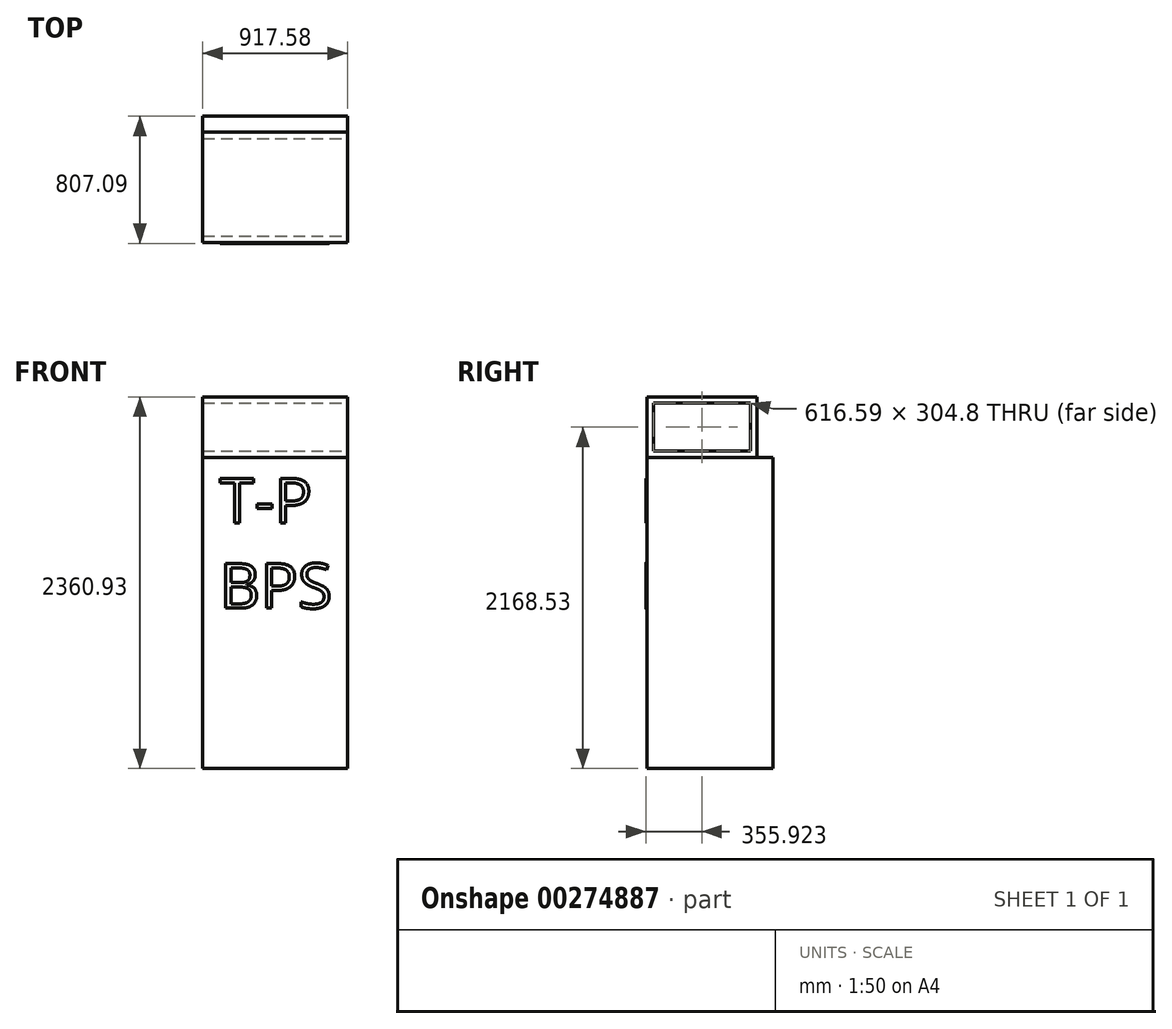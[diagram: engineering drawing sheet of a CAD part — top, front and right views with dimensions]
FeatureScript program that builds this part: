
annotation { "Feature Type Name" : "Feature", "Feature Type Description" : "" }
export const myFeature = defineFeature(function(context is Context, id is Id, definition is map)
    precondition{}
    {
        {
            var Q0;
            Q0=qCreatedBy(makeId("Top.planeOp"),FACE);
            var sketch = newSketch(context, id + "F0", { "sketchPlane" : qUnion([Q0])});
            skLineSegment(sketch, "E0.bottom", {"start": v(0, 0) * mm, "end": v(917.58, 0) * mm});
            skLineSegment(sketch, "E0.top", {"start": v(0, -800.74) * mm, "end": v(917.58, -800.74) * mm});
            skLineSegment(sketch, "E0.left", {"start": v(0, 0) * mm, "end": v(0, -800.74) * mm});
            skLineSegment(sketch, "E0.right", {"start": v(917.58, 0) * mm, "end": v(917.58, -800.74) * mm});
            skSolve(sketch);
        }
        {
            var Q0;
            Q0=makeQuery(id+"F0.imprint","IMPRINT",FACE,{"disambiguationData":[TD([[makeQuery(id+"F0.imprint","IMPRINT",EDGE,{"derivedFrom":sQuery(id+"F0.wireOp",EDGE,"E0.bottom")}),-1.0]])]});
            extrude(context, id + "F1", {"entities" : qUnion([Q0]), "depth" : 1974.85 * mm});
        }
        {
            var Q0;
            Q0=makeQuery(id+"F1.opExtrude","SWEPT_FACE",FACE,{"disambiguationData":[OSD([sQuery(id+"F0.wireOp",EDGE,"E0.top")])]});
            var sketch = newSketch(context, id + "F2", { "sketchPlane" : qUnion([Q0])});
            skText(sketch, "E1", { "text": "T-P\nBPS", "fontName": "OpenSans-Regular.ttf"});
            const initialGuessF2  = {"E1": [0.10689, 1.55914, 1, 0, 0.28607]};
            skSetInitialGuess(sketch, initialGuessF2);
            skSolve(sketch);
        }
        {
            var Q0;
            Q0 = qSketchRegion(id + "F2", true);
            extrude(context, id + "F3", {"entities" : qUnion([Q0]), "operationType" : NewBodyOperationType.ADD, "depth" : 6.35 * mm});
        }
        {
            var Q0;
            Q0=makeQuery(id+"F1.opExtrude","CAP_FACE",FACE,{"disambiguationData":[OSD([sQuery(id+"F0.wireOp",EDGE,"E0.bottom"),sQuery(id+"F0.wireOp",EDGE,"E0.top"),sQuery(id+"F0.wireOp",EDGE,"E0.left"),sQuery(id+"F0.wireOp",EDGE,"E0.right")])],"isStart":false});
            var sketch = newSketch(context, id + "F4", { "sketchPlane" : qUnion([Q0])});
            skLineSegment(sketch, "E2.bottom", {"start": v(0, 0) * mm, "end": v(917.58, 0) * mm});
            skLineSegment(sketch, "E2.top", {"start": v(0, -800.74) * mm, "end": v(917.58, -800.74) * mm});
            skLineSegment(sketch, "E2.left", {"start": v(0, 0) * mm, "end": v(0, -800.74) * mm});
            skLineSegment(sketch, "E2.right", {"start": v(917.58, 0) * mm, "end": v(917.58, -800.74) * mm});
            skSolve(sketch);
        }
        {
            var Q0;
            Q0=makeQuery(id+"F4.imprint","IMPRINT",FACE,{"disambiguationData":[TD([[makeQuery(id+"F4.imprint","IMPRINT",EDGE,{"derivedFrom":sQuery(id+"F4.wireOp",EDGE,"E2.bottom")}),-1.0]])]});
            extrude(context, id + "F5", {"entities" : qUnion([Q0]), "depth" : 508 * mm, "offsetDistance" : 25.4 * mm});
        }
        {
            var Q0;
            Q0=makeQuery(id+"F1.opExtrude","SWEPT_FACE",FACE,{"disambiguationData":[OSD([sQuery(id+"F0.wireOp",EDGE,"E0.right")])]});
            var sketch = newSketch(context, id + "F6", { "sketchPlane" : qUnion([Q0])});
            skLineSegment(sketch, "E3", {"start": v(0, 0) * mm, "end": v(0, 2016.13) * mm, "construction": true});
            skLineSegment(sketch, "E4", {"start": v(0, 2016.13) * mm, "end": v(-41.28, 2016.13) * mm, "construction": true});
            skLineSegment(sketch, "E5.bottom", {"start": v(-800.74, 1974.85) * mm, "end": v(-759.46, 1974.85) * mm, "construction": true});
            skLineSegment(sketch, "E5.top", {"start": v(-800.74, 2016.13) * mm, "end": v(-759.46, 2016.13) * mm, "construction": true});
            skLineSegment(sketch, "E5.left", {"start": v(-800.74, 1974.85) * mm, "end": v(-800.74, 2016.13) * mm, "construction": true});
            skLineSegment(sketch, "E5.right", {"start": v(-759.46, 1974.85) * mm, "end": v(-759.46, 2016.13) * mm, "construction": true});
            skLineSegment(sketch, "E6.bottom", {"start": v(-41.28, 2016.13) * mm, "end": v(-759.46, 2016.13) * mm});
            skLineSegment(sketch, "E6.top", {"start": v(-41.28, 2320.93) * mm, "end": v(-759.46, 2320.93) * mm});
            skLineSegment(sketch, "E6.left", {"start": v(-41.28, 2016.13) * mm, "end": v(-41.28, 2320.93) * mm});
            skLineSegment(sketch, "E6.right", {"start": v(-759.46, 2016.13) * mm, "end": v(-759.46, 2320.93) * mm});
            skSolve(sketch);
        }
        {
            var Q0;
            Q0=makeQuery(id+"F6.imprint","IMPRINT",FACE,{"disambiguationData":[TD([[makeQuery(id+"F6.imprint","IMPRINT",EDGE,{"derivedFrom":sQuery(id+"F6.wireOp",EDGE,"E6.bottom")}),-1.0]])]});
            extrude(context, id + "F7", {"entities" : qUnion([Q0]), "operationType" : NewBodyOperationType.REMOVE, "oppositeDirection" : true, "depth" : 1155.7 * mm, "offsetDistance" : 25.4 * mm});
        }
        {
            var Q0;
            Q0=makeQuery(id+"F5.opExtrude","CAP_FACE",FACE,{"disambiguationData":[OSD([sQuery(id+"F4.wireOp",EDGE,"E2.bottom"),sQuery(id+"F4.wireOp",EDGE,"E2.top"),sQuery(id+"F4.wireOp",EDGE,"E2.left"),sQuery(id+"F4.wireOp",EDGE,"E2.right")])],"isStart":false});
            extrude(context, id + "F8", {"entities" : qUnion([Q0]), "operationType" : NewBodyOperationType.REMOVE, "oppositeDirection" : true, "depth" : 121.92 * mm, "offsetDistance" : 25.4 * mm});
        }
        {
            var Q0;
            Q0=makeQuery(id+"F7.boolean.opBoolean","COPY",FACE,{"derivedFrom":makeQuery(id+"F7.opExtrude","SWEPT_FACE",FACE,{"disambiguationData":[OSD([sQuery(id+"F6.wireOp",EDGE,"E6.left")])]})});
            extrude(context, id + "F9", {"entities" : qUnion([Q0]), "operationType" : NewBodyOperationType.ADD, "depth" : 101.6 * mm, "offsetDistance" : 25.4 * mm});
        }
        {
            var Q0;
            Q0=makeQuery(id+"F5.opExtrude","SWEPT_FACE",FACE,{"disambiguationData":[OSD([sQuery(id+"F4.wireOp",EDGE,"E2.bottom")])]});
            extrude(context, id + "F10", {"entities" : qUnion([Q0]), "operationType" : NewBodyOperationType.REMOVE, "oppositeDirection" : true, "depth" : 101.6 * mm, "offsetDistance" : 25.4 * mm});
        }
    });
